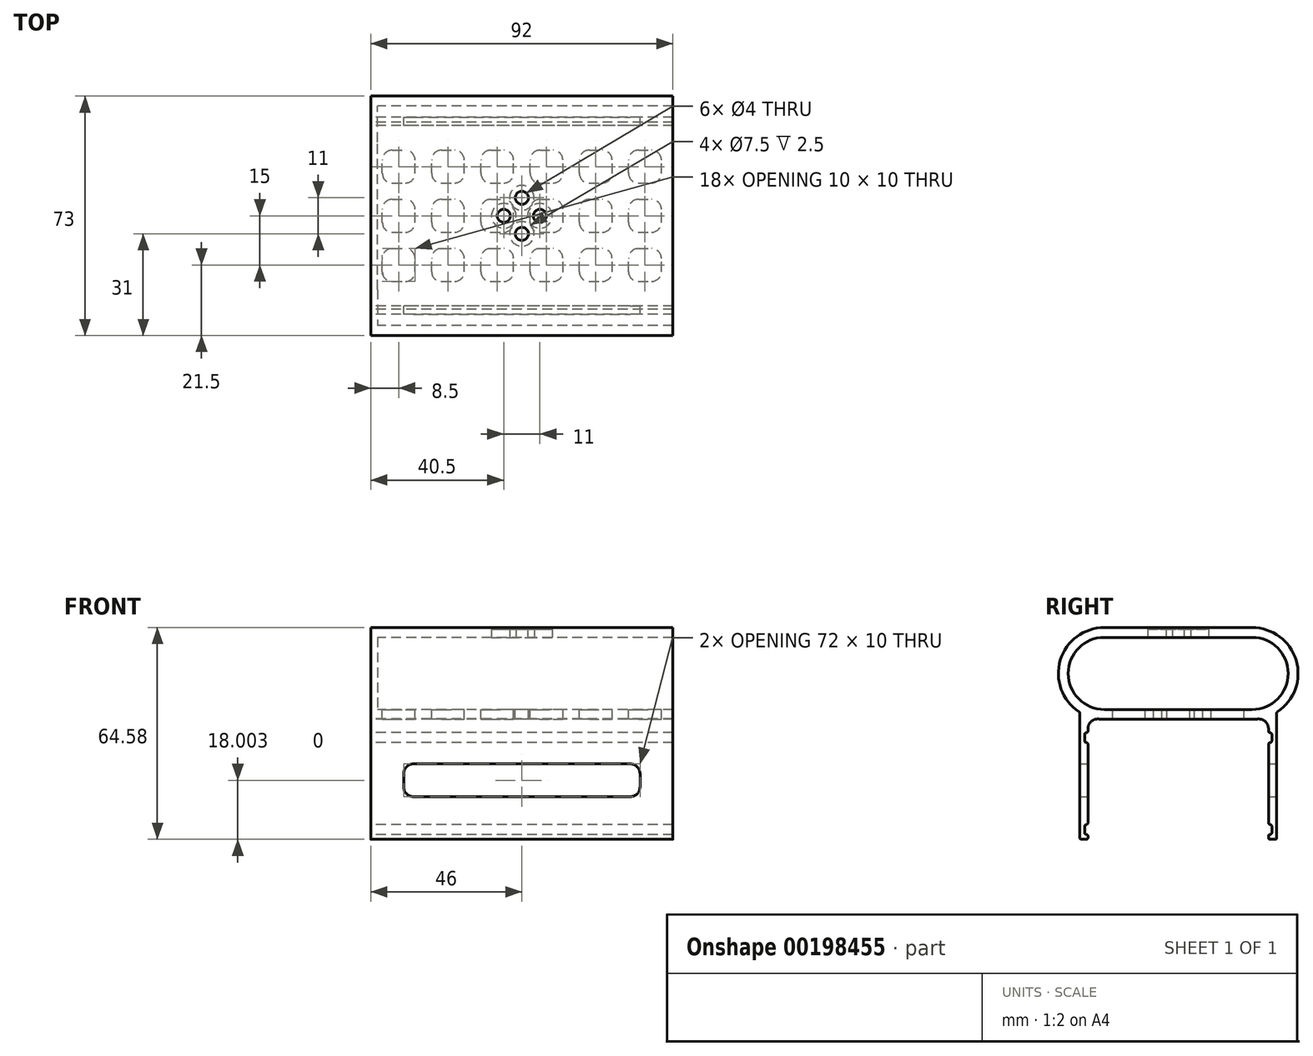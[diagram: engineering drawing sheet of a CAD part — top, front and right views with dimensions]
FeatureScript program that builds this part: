
annotation { "Feature Type Name" : "Feature", "Feature Type Description" : "" }
export const myFeature = defineFeature(function(context is Context, id is Id, definition is map)
    precondition{}
    {
        {
            var Q0;
            Q0=qCreatedBy(makeId("Right.planeOp"),FACE);
            var sketch = newSketch(context, id + "F0", { "sketchPlane" : qUnion([Q0])});
            skLineSegment(sketch, "E0.bottom", {"start": v(-22.5, 0) * mm, "end": v(22.5, 0) * mm});
            skLineSegment(sketch, "E0.top", {"start": v(-22.5, 22) * mm, "end": v(22.5, 22) * mm});
            skLineSegment(sketch, "E0.left", {"start": v(-33.5, 11) * mm, "end": v(-33.5, 11) * mm});
            skLineSegment(sketch, "E0.right", {"start": v(33.5, 11) * mm, "end": v(33.5, 11) * mm});
            skPoint(sketch, "E1.visualSharp", {"position": v(-33.5, 22) * mm});
            skArc(sketch, "E1.filletArc", {"start": v(-22.5, 22) * mm, "mid": v(-30.28, 18.78) * mm, "end": v(-33.5, 11) * mm});
            skPoint(sketch, "E2.visualSharp", {"position": v(-33.5, 0) * mm});
            skArc(sketch, "E2.filletArc", {"start": v(-33.5, 11) * mm, "mid": v(-30.28, 3.22) * mm, "end": v(-22.5, 0) * mm});
            skPoint(sketch, "E3.visualSharp", {"position": v(33.5, 0) * mm});
            skArc(sketch, "E3.filletArc", {"start": v(22.5, 0) * mm, "mid": v(30.28, 3.22) * mm, "end": v(33.5, 11) * mm});
            skPoint(sketch, "E4.visualSharp", {"position": v(33.5, 22) * mm});
            skArc(sketch, "E4.filletArc", {"start": v(33.5, 11) * mm, "mid": v(30.28, 18.78) * mm, "end": v(22.5, 22) * mm});
            skLineSegment(sketch, "E5.0", {"start": v(-22.5, 25) * mm, "end": v(22.5, 25) * mm});
            skArc(sketch, "E5.1", {"start": v(-36.5, 11) * mm, "mid": v(-34.83, 4.37) * mm, "end": v(-30.22, -0.68) * mm});
            skLineSegment(sketch, "E5.2", {"start": v(-22.5, -3) * mm, "end": v(22.5, -3) * mm});
            skArc(sketch, "E5.3", {"start": v(-22.5, 25) * mm, "mid": v(-32.4, 20.9) * mm, "end": v(-36.5, 11) * mm});
            skArc(sketch, "E5.5", {"start": v(36.5, 11) * mm, "mid": v(32.4, 20.9) * mm, "end": v(22.5, 25) * mm});
            skLineSegment(sketch, "E6", {"start": v(-28.5, -1.65) * mm, "end": v(-28.5, -38.08) * mm, "construction": true});
            skLineSegment(sketch, "E7", {"start": v(-28.5, -38.08) * mm, "end": v(28.5, -38.08) * mm, "construction": true});
            skLineSegment(sketch, "E8", {"start": v(28.5, -38.08) * mm, "end": v(28.5, -1.65) * mm, "construction": true});
            skLineSegment(sketch, "E9", {"start": v(0, 0) * mm, "end": v(0, -38.08) * mm, "construction": true});
            skLineSegment(sketch, "E10", {"start": v(-28, -7.08) * mm, "end": v(-28, -7.08) * mm});
            skLineSegment(sketch, "E11", {"start": v(-27.5, -6.58) * mm, "end": v(-27.5, -5.88) * mm});
            skLineSegment(sketch, "E12", {"start": v(-28, -35.08) * mm, "end": v(-28, -35.08) * mm});
            skLineSegment(sketch, "E13", {"start": v(-27.5, -34.58) * mm, "end": v(-27.5, -10.58) * mm});
            skLineSegment(sketch, "E14", {"start": v(-28, -10.08) * mm, "end": v(-28, -10.08) * mm});
            skLineSegment(sketch, "E15", {"start": v(-28, -38.08) * mm, "end": v(-28, -38.08) * mm});
            skLineSegment(sketch, "E16", {"start": v(-27.5, -38.58) * mm, "end": v(-27.5, -39.08) * mm});
            skLineSegment(sketch, "E17", {"start": v(-28, -39.58) * mm, "end": v(-29.5, -39.58) * mm});
            skLineSegment(sketch, "E18", {"start": v(-30, -39.08) * mm, "end": v(-30, -1.1) * mm});
            skLineSegment(sketch, "E19", {"start": v(-28.5, -7.58) * mm, "end": v(-28.5, -9.58) * mm});
            skLineSegment(sketch, "E20", {"start": v(-28.5, -35.58) * mm, "end": v(-28.5, -37.58) * mm});
            skArc(sketch, "E21.trimOffspring", {"start": v(-24.15, -2.9) * mm, "mid": v(-23.32, -2.98) * mm, "end": v(-22.5, -3) * mm});
            skPoint(sketch, "E22.visualSharp", {"position": v(-30, -0.82) * mm});
            skArc(sketch, "E22.filletArc", {"start": v(-30, -1.1) * mm, "mid": v(-30.06, -0.86) * mm, "end": v(-30.22, -0.68) * mm});
            skPoint(sketch, "E23.visualSharp", {"position": v(-27.5, -2.08) * mm});
            skArc(sketch, "E23.filletArc", {"start": v(-24.15, -2.9) * mm, "mid": v(-26.5, -3.64) * mm, "end": v(-27.5, -5.88) * mm});
            skPoint(sketch, "E24.visualSharp", {"position": v(-28.5, -7.08) * mm});
            skArc(sketch, "E24.filletArc", {"start": v(-28, -7.08) * mm, "mid": v(-28.35, -7.22) * mm, "end": v(-28.5, -7.58) * mm});
            skPoint(sketch, "E25.visualSharp", {"position": v(-28.5, -10.08) * mm});
            skArc(sketch, "E25.filletArc", {"start": v(-28.5, -9.58) * mm, "mid": v(-28.35, -9.93) * mm, "end": v(-28, -10.08) * mm});
            skPoint(sketch, "E26.visualSharp", {"position": v(-27.5, -10.08) * mm});
            skArc(sketch, "E26.filletArc", {"start": v(-27.5, -10.58) * mm, "mid": v(-27.65, -10.22) * mm, "end": v(-28, -10.08) * mm});
            skPoint(sketch, "E27.visualSharp", {"position": v(-27.5, -7.08) * mm});
            skArc(sketch, "E27.filletArc", {"start": v(-28, -7.08) * mm, "mid": v(-27.65, -6.93) * mm, "end": v(-27.5, -6.58) * mm});
            skPoint(sketch, "E28.visualSharp", {"position": v(-27.5, -35.08) * mm});
            skArc(sketch, "E28.filletArc", {"start": v(-28, -35.08) * mm, "mid": v(-27.65, -34.93) * mm, "end": v(-27.5, -34.58) * mm});
            skPoint(sketch, "E29.visualSharp", {"position": v(-28.5, -35.08) * mm});
            skArc(sketch, "E29.filletArc", {"start": v(-28, -35.08) * mm, "mid": v(-28.35, -35.22) * mm, "end": v(-28.5, -35.58) * mm});
            skPoint(sketch, "E30.visualSharp", {"position": v(-28.5, -38.08) * mm});
            skArc(sketch, "E30.filletArc", {"start": v(-28.5, -37.58) * mm, "mid": v(-28.35, -37.93) * mm, "end": v(-28, -38.08) * mm});
            skPoint(sketch, "E31.visualSharp", {"position": v(-27.5, -38.08) * mm});
            skArc(sketch, "E31.filletArc", {"start": v(-27.5, -38.58) * mm, "mid": v(-27.65, -38.22) * mm, "end": v(-28, -38.08) * mm});
            skPoint(sketch, "E32.visualSharp", {"position": v(-27.5, -39.58) * mm});
            skArc(sketch, "E32.filletArc", {"start": v(-28, -39.58) * mm, "mid": v(-27.65, -39.43) * mm, "end": v(-27.5, -39.08) * mm});
            skPoint(sketch, "E33.visualSharp", {"position": v(-30, -39.58) * mm});
            skArc(sketch, "E33.filletArc", {"start": v(-30, -39.08) * mm, "mid": v(-29.85, -39.43) * mm, "end": v(-29.5, -39.58) * mm});
            skArc(sketch, "E34.MirrorCS", {"start": v(27.5, -38.58) * mm, "mid": v(27.65, -38.22) * mm, "end": v(28, -38.08) * mm});
            skArc(sketch, "E35.MirrorCS", {"start": v(28.5, -37.58) * mm, "mid": v(28.35, -37.93) * mm, "end": v(28, -38.08) * mm});
            skLineSegment(sketch, "E36.MirrorCS", {"start": v(28.5, -35.58) * mm, "end": v(28.5, -37.58) * mm});
            skArc(sketch, "E37.MirrorCS", {"start": v(28, -35.08) * mm, "mid": v(28.35, -35.22) * mm, "end": v(28.5, -35.58) * mm});
            skLineSegment(sketch, "E38.MirrorCS", {"start": v(27.5, -38.58) * mm, "end": v(27.5, -39.08) * mm});
            skArc(sketch, "E39.MirrorCS", {"start": v(28, -39.58) * mm, "mid": v(27.65, -39.43) * mm, "end": v(27.5, -39.08) * mm});
            skLineSegment(sketch, "E40.MirrorCS", {"start": v(28, -39.58) * mm, "end": v(29.5, -39.58) * mm});
            skArc(sketch, "E41.MirrorCS", {"start": v(28, -35.08) * mm, "mid": v(27.65, -34.93) * mm, "end": v(27.5, -34.58) * mm});
            skArc(sketch, "E42.MirrorCS", {"start": v(30, -1.1) * mm, "mid": v(30.06, -0.86) * mm, "end": v(30.22, -0.68) * mm});
            skLineSegment(sketch, "E43.MirrorCS", {"start": v(27.5, -6.58) * mm, "end": v(27.5, -5.88) * mm});
            skArc(sketch, "E44.MirrorCS", {"start": v(28, -7.08) * mm, "mid": v(27.65, -6.93) * mm, "end": v(27.5, -6.58) * mm});
            skArc(sketch, "E45.MirrorCS", {"start": v(28.5, -9.58) * mm, "mid": v(28.35, -9.93) * mm, "end": v(28, -10.08) * mm});
            skArc(sketch, "E46.MirrorCS", {"start": v(30, -39.08) * mm, "mid": v(29.85, -39.43) * mm, "end": v(29.5, -39.58) * mm});
            skArc(sketch, "E47.MirrorCS", {"start": v(28, -7.08) * mm, "mid": v(28.35, -7.22) * mm, "end": v(28.5, -7.58) * mm});
            skLineSegment(sketch, "E48.MirrorCS", {"start": v(28.5, -7.58) * mm, "end": v(28.5, -9.58) * mm});
            skArc(sketch, "E49.MirrorCS", {"start": v(27.5, -10.58) * mm, "mid": v(27.65, -10.22) * mm, "end": v(28, -10.08) * mm});
            skArc(sketch, "E50.MirrorCS", {"start": v(24.15, -2.9) * mm, "mid": v(23.32, -2.98) * mm, "end": v(22.5, -3) * mm});
            skPoint(sketch, "E51.MirrorP", {"position": v(30, -39.58) * mm});
            skPoint(sketch, "E52.MirrorP", {"position": v(28.5, -38.08) * mm});
            skPoint(sketch, "E53.MirrorP", {"position": v(27.5, -2.08) * mm});
            skPoint(sketch, "E54.MirrorP", {"position": v(27.5, -38.08) * mm});
            skLineSegment(sketch, "E55.MirrorCS", {"start": v(28.5, -1.65) * mm, "end": v(28.5, -38.08) * mm, "construction": true});
            skPoint(sketch, "E56.MirrorP", {"position": v(28.5, -10.08) * mm});
            skLineSegment(sketch, "E57.MirrorCS", {"start": v(30, -39.08) * mm, "end": v(30, -1.1) * mm});
            skLineSegment(sketch, "E58.MirrorCS", {"start": v(28, -35.08) * mm, "end": v(28, -35.08) * mm});
            skPoint(sketch, "E59.MirrorP", {"position": v(27.5, -10.08) * mm});
            skLineSegment(sketch, "E60.MirrorCS", {"start": v(28, -7.08) * mm, "end": v(28, -7.08) * mm});
            skPoint(sketch, "E61.MirrorP", {"position": v(27.5, -7.08) * mm});
            skLineSegment(sketch, "E62.MirrorCS", {"start": v(28, -38.08) * mm, "end": v(28, -38.08) * mm});
            skArc(sketch, "E63.MirrorCS", {"start": v(24.15, -2.9) * mm, "mid": v(26.5, -3.64) * mm, "end": v(27.5, -5.88) * mm});
            skPoint(sketch, "E64.MirrorP", {"position": v(27.5, -39.58) * mm});
            skPoint(sketch, "E65.MirrorP", {"position": v(28.5, -7.08) * mm});
            skPoint(sketch, "E66.MirrorP", {"position": v(28.5, -35.08) * mm});
            skLineSegment(sketch, "E67.MirrorCS", {"start": v(27.5, -34.58) * mm, "end": v(27.5, -10.58) * mm});
            skPoint(sketch, "E68.MirrorP", {"position": v(27.5, -35.08) * mm});
            skLineSegment(sketch, "E69.MirrorCS", {"start": v(28, -10.08) * mm, "end": v(28, -10.08) * mm});
            skPoint(sketch, "E70.MirrorP", {"position": v(30, -0.82) * mm});
            skArc(sketch, "E71.trimOffspring", {"start": v(30, -0.82) * mm, "mid": v(34.77, 4.25) * mm, "end": v(36.5, 11) * mm});
            skSolve(sketch);
        }
        {
            var Q0;
            Q0 = qSketchRegion(id + "F0", true);
            extrude(context, id + "F1", {"entities" : qUnion([Q0]), "depth" : 90 * mm});
        }
        {
            var Q0;
            Q0=makeQuery(id+"F1.opExtrude","CAP_FACE",FACE,{"disambiguationData":[OSD([sQuery(id+"F0.wireOp",EDGE,"E0.bottom"),sQuery(id+"F0.wireOp",EDGE,"E0.top"),sQuery(id+"F0.wireOp",EDGE,"E1.filletArc"),sQuery(id+"F0.wireOp",EDGE,"E2.filletArc"),sQuery(id+"F0.wireOp",EDGE,"E3.filletArc"),sQuery(id+"F0.wireOp",EDGE,"E4.filletArc"),sQuery(id+"F0.wireOp",EDGE,"E5.0"),sQuery(id+"F0.wireOp",EDGE,"E5.1"),sQuery(id+"F0.wireOp",EDGE,"E5.2"),sQuery(id+"F0.wireOp",EDGE,"E5.3"),sQuery(id+"F0.wireOp",EDGE,"E5.4"),sQuery(id+"F0.wireOp",EDGE,"E5.5")])],"isStart":true});
            var sketch = newSketch(context, id + "F2", { "sketchPlane" : qUnion([Q0])});
            skArc(sketch, "E72.0", {"start": v(-30.22, -0.68) * mm, "mid": v(-35.9, 15.03) * mm, "end": v(-22.5, 25) * mm});
            skArc(sketch, "E73.0.0", {"start": v(-30.22, -0.68) * mm, "mid": v(-30.06, -0.86) * mm, "end": v(-30, -1.1) * mm});
            skLineSegment(sketch, "E73.0.1", {"start": v(-30, -1.1) * mm, "end": v(-30, -39.08) * mm});
            skArc(sketch, "E73.0.2", {"start": v(-30, -39.08) * mm, "mid": v(-29.85, -39.43) * mm, "end": v(-29.5, -39.58) * mm});
            skLineSegment(sketch, "E73.0.3", {"start": v(-29.5, -39.58) * mm, "end": v(-28, -39.58) * mm});
            skArc(sketch, "E73.0.4", {"start": v(-28, -39.58) * mm, "mid": v(-27.65, -39.43) * mm, "end": v(-27.5, -39.08) * mm});
            skLineSegment(sketch, "E73.0.5", {"start": v(-27.5, -39.08) * mm, "end": v(-27.5, -38.58) * mm});
            skArc(sketch, "E73.0.6", {"start": v(-27.5, -38.58) * mm, "mid": v(-27.65, -38.22) * mm, "end": v(-28, -38.08) * mm});
            skArc(sketch, "E73.0.7", {"start": v(-28, -38.08) * mm, "mid": v(-28.35, -37.93) * mm, "end": v(-28.5, -37.58) * mm});
            skLineSegment(sketch, "E73.0.8", {"start": v(-28.5, -37.58) * mm, "end": v(-28.5, -35.58) * mm});
            skArc(sketch, "E73.0.9", {"start": v(-28.5, -35.58) * mm, "mid": v(-28.35, -35.22) * mm, "end": v(-28, -35.08) * mm});
            skArc(sketch, "E73.0.10", {"start": v(-28, -35.08) * mm, "mid": v(-27.65, -34.93) * mm, "end": v(-27.5, -34.58) * mm});
            skLineSegment(sketch, "E73.0.11", {"start": v(-27.5, -34.58) * mm, "end": v(-27.5, -10.58) * mm});
            skArc(sketch, "E73.0.12", {"start": v(-27.5, -10.58) * mm, "mid": v(-27.65, -10.22) * mm, "end": v(-28, -10.08) * mm});
            skArc(sketch, "E73.0.13", {"start": v(-28, -10.08) * mm, "mid": v(-28.35, -9.93) * mm, "end": v(-28.5, -9.58) * mm});
            skLineSegment(sketch, "E73.0.14", {"start": v(-28.5, -9.58) * mm, "end": v(-28.5, -7.58) * mm});
            skArc(sketch, "E73.0.15", {"start": v(-28.5, -7.58) * mm, "mid": v(-28.35, -7.22) * mm, "end": v(-28, -7.08) * mm});
            skArc(sketch, "E73.0.16", {"start": v(-28, -7.08) * mm, "mid": v(-27.65, -6.93) * mm, "end": v(-27.5, -6.58) * mm});
            skLineSegment(sketch, "E73.0.17", {"start": v(-27.5, -6.58) * mm, "end": v(-27.5, -5.88) * mm});
            skArc(sketch, "E73.0.18", {"start": v(-27.5, -5.88) * mm, "mid": v(-26.5, -3.64) * mm, "end": v(-24.15, -2.9) * mm});
            skArc(sketch, "E73.0.19", {"start": v(-24.15, -2.9) * mm, "mid": v(-23.32, -2.98) * mm, "end": v(-22.5, -3) * mm});
            skLineSegment(sketch, "E73.0.20", {"start": v(-22.5, -3) * mm, "end": v(22.5, -3) * mm});
            skArc(sketch, "E73.0.21", {"start": v(22.5, -3) * mm, "mid": v(23.32, -2.98) * mm, "end": v(24.15, -2.9) * mm});
            skArc(sketch, "E73.0.22", {"start": v(24.15, -2.9) * mm, "mid": v(26.5, -3.64) * mm, "end": v(27.5, -5.88) * mm});
            skLineSegment(sketch, "E73.0.23", {"start": v(27.5, -5.88) * mm, "end": v(27.5, -6.58) * mm});
            skArc(sketch, "E73.0.24", {"start": v(27.5, -6.58) * mm, "mid": v(27.65, -6.93) * mm, "end": v(28, -7.08) * mm});
            skArc(sketch, "E73.0.25", {"start": v(28, -7.08) * mm, "mid": v(28.35, -7.22) * mm, "end": v(28.5, -7.58) * mm});
            skLineSegment(sketch, "E73.0.26", {"start": v(28.5, -7.58) * mm, "end": v(28.5, -9.58) * mm});
            skArc(sketch, "E73.0.27", {"start": v(28.5, -9.58) * mm, "mid": v(28.35, -9.93) * mm, "end": v(28, -10.08) * mm});
            skArc(sketch, "E73.0.28", {"start": v(28, -10.08) * mm, "mid": v(27.65, -10.22) * mm, "end": v(27.5, -10.58) * mm});
            skLineSegment(sketch, "E73.0.29", {"start": v(27.5, -10.58) * mm, "end": v(27.5, -34.58) * mm});
            skArc(sketch, "E73.0.30", {"start": v(27.5, -34.58) * mm, "mid": v(27.65, -34.93) * mm, "end": v(28, -35.08) * mm});
            skArc(sketch, "E73.0.31", {"start": v(28, -35.08) * mm, "mid": v(28.35, -35.22) * mm, "end": v(28.5, -35.58) * mm});
            skLineSegment(sketch, "E73.0.32", {"start": v(28.5, -35.58) * mm, "end": v(28.5, -37.58) * mm});
            skArc(sketch, "E73.0.33", {"start": v(28.5, -37.58) * mm, "mid": v(28.35, -37.93) * mm, "end": v(28, -38.08) * mm});
            skArc(sketch, "E73.0.34", {"start": v(28, -38.08) * mm, "mid": v(27.65, -38.22) * mm, "end": v(27.5, -38.58) * mm});
            skLineSegment(sketch, "E73.0.35", {"start": v(27.5, -38.58) * mm, "end": v(27.5, -39.08) * mm});
            skArc(sketch, "E73.0.36", {"start": v(27.5, -39.08) * mm, "mid": v(27.65, -39.43) * mm, "end": v(28, -39.58) * mm});
            skLineSegment(sketch, "E73.0.37", {"start": v(28, -39.58) * mm, "end": v(29.5, -39.58) * mm});
            skArc(sketch, "E73.0.38", {"start": v(29.5, -39.58) * mm, "mid": v(29.85, -39.43) * mm, "end": v(30, -39.08) * mm});
            skLineSegment(sketch, "E73.0.39", {"start": v(30, -39.08) * mm, "end": v(30, -1.1) * mm});
            skArc(sketch, "E73.0.40", {"start": v(30, -1.1) * mm, "mid": v(30.06, -0.86) * mm, "end": v(30.22, -0.68) * mm});
            skArc(sketch, "E73.0.41", {"start": v(30.22, -0.68) * mm, "mid": v(35.9, 15.03) * mm, "end": v(22.5, 25) * mm});
            skLineSegment(sketch, "E73.0.42", {"start": v(22.5, 25) * mm, "end": v(-22.5, 25) * mm});
            skArc(sketch, "E73.0.43", {"start": v(-22.5, 25) * mm, "mid": v(-35.9, 15.03) * mm, "end": v(-30.22, -0.68) * mm});
            skSolve(sketch);
        }
        {
            var Q0;
            Q0 = qSketchRegion(id + "F2", true);
            extrude(context, id + "F3", {"entities" : qUnion([Q0]), "operationType" : NewBodyOperationType.ADD, "depth" : 2 * mm});
        }
        {
            var Q0;
            Q0=qCreatedBy(makeId("Top.planeOp"),FACE);
            var sketch = newSketch(context, id + "F4", { "sketchPlane" : qUnion([Q0])});
            skLineSegment(sketch, "E74.bottom", {"start": v(4.5, -5) * mm, "end": v(8.5, -5) * mm});
            skLineSegment(sketch, "E74.top", {"start": v(4.5, 5) * mm, "end": v(8.5, 5) * mm});
            skLineSegment(sketch, "E74.left", {"start": v(1.5, -2) * mm, "end": v(1.5, 2) * mm});
            skLineSegment(sketch, "E74.right", {"start": v(11.5, -2) * mm, "end": v(11.5, 2) * mm});
            skPoint(sketch, "E74.middle", {"position": v(6.5, 0) * mm});
            skPoint(sketch, "E75.visualSharp", {"position": v(1.5, 5) * mm});
            skArc(sketch, "E75.filletArc", {"start": v(4.5, 5) * mm, "mid": v(2.38, 4.12) * mm, "end": v(1.5, 2) * mm});
            skPoint(sketch, "E76.visualSharp", {"position": v(11.5, 5) * mm});
            skArc(sketch, "E76.filletArc", {"start": v(11.5, 2) * mm, "mid": v(10.62, 4.12) * mm, "end": v(8.5, 5) * mm});
            skPoint(sketch, "E77.visualSharp", {"position": v(11.5, -5) * mm});
            skArc(sketch, "E77.filletArc", {"start": v(8.5, -5) * mm, "mid": v(10.62, -4.12) * mm, "end": v(11.5, -2) * mm});
            skPoint(sketch, "E78.visualSharp", {"position": v(1.5, -5) * mm});
            skArc(sketch, "E78.filletArc", {"start": v(1.5, -2) * mm, "mid": v(2.38, -4.12) * mm, "end": v(4.5, -5) * mm});
            skPoint(sketch, "E79.0.1.0", {"position": v(1.5, 20) * mm});
            skLineSegment(sketch, "E79.0.1.1", {"start": v(1.5, 13) * mm, "end": v(1.5, 17) * mm});
            skLineSegment(sketch, "E79.0.1.2", {"start": v(11.5, 13) * mm, "end": v(11.5, 17) * mm});
            skPoint(sketch, "E79.0.1.3", {"position": v(11.5, 20) * mm});
            skPoint(sketch, "E79.0.1.4", {"position": v(6.5, 15) * mm});
            skPoint(sketch, "E79.0.1.5", {"position": v(11.5, 10) * mm});
            skPoint(sketch, "E79.0.1.6", {"position": v(1.5, 10) * mm});
            skArc(sketch, "E79.0.1.7", {"start": v(4.5, 20) * mm, "mid": v(2.38, 19.12) * mm, "end": v(1.5, 17) * mm});
            skArc(sketch, "E79.0.1.8", {"start": v(1.5, 13) * mm, "mid": v(2.38, 10.88) * mm, "end": v(4.5, 10) * mm});
            skLineSegment(sketch, "E79.0.1.9", {"start": v(4.5, 10) * mm, "end": v(8.5, 10) * mm});
            skLineSegment(sketch, "E79.0.1.10", {"start": v(4.5, 20) * mm, "end": v(8.5, 20) * mm});
            skArc(sketch, "E79.0.1.11", {"start": v(11.5, 17) * mm, "mid": v(10.62, 19.12) * mm, "end": v(8.5, 20) * mm});
            skArc(sketch, "E79.0.1.12", {"start": v(8.5, 10) * mm, "mid": v(10.62, 10.88) * mm, "end": v(11.5, 13) * mm});
            skPoint(sketch, "E79.1.0.0", {"position": v(16.5, 5) * mm});
            skLineSegment(sketch, "E79.1.0.1", {"start": v(16.5, -2) * mm, "end": v(16.5, 2) * mm});
            skLineSegment(sketch, "E79.1.0.2", {"start": v(26.5, -2) * mm, "end": v(26.5, 2) * mm});
            skPoint(sketch, "E79.1.0.3", {"position": v(26.5, 5) * mm});
            skPoint(sketch, "E79.1.0.4", {"position": v(21.5, 0) * mm});
            skPoint(sketch, "E79.1.0.5", {"position": v(26.5, -5) * mm});
            skPoint(sketch, "E79.1.0.6", {"position": v(16.5, -5) * mm});
            skArc(sketch, "E79.1.0.7", {"start": v(19.5, 5) * mm, "mid": v(17.38, 4.12) * mm, "end": v(16.5, 2) * mm});
            skArc(sketch, "E79.1.0.8", {"start": v(16.5, -2) * mm, "mid": v(17.38, -4.12) * mm, "end": v(19.5, -5) * mm});
            skLineSegment(sketch, "E79.1.0.9", {"start": v(19.5, -5) * mm, "end": v(23.5, -5) * mm});
            skLineSegment(sketch, "E79.1.0.10", {"start": v(19.5, 5) * mm, "end": v(23.5, 5) * mm});
            skArc(sketch, "E79.1.0.11", {"start": v(26.5, 2) * mm, "mid": v(25.62, 4.12) * mm, "end": v(23.5, 5) * mm});
            skArc(sketch, "E79.1.0.12", {"start": v(23.5, -5) * mm, "mid": v(25.62, -4.12) * mm, "end": v(26.5, -2) * mm});
            skPoint(sketch, "E79.1.1.0", {"position": v(16.5, 20) * mm});
            skLineSegment(sketch, "E79.1.1.1", {"start": v(16.5, 13) * mm, "end": v(16.5, 17) * mm});
            skLineSegment(sketch, "E79.1.1.2", {"start": v(26.5, 13) * mm, "end": v(26.5, 17) * mm});
            skPoint(sketch, "E79.1.1.3", {"position": v(26.5, 20) * mm});
            skPoint(sketch, "E79.1.1.4", {"position": v(21.5, 15) * mm});
            skPoint(sketch, "E79.1.1.5", {"position": v(26.5, 10) * mm});
            skPoint(sketch, "E79.1.1.6", {"position": v(16.5, 10) * mm});
            skArc(sketch, "E79.1.1.7", {"start": v(19.5, 20) * mm, "mid": v(17.38, 19.12) * mm, "end": v(16.5, 17) * mm});
            skArc(sketch, "E79.1.1.8", {"start": v(16.5, 13) * mm, "mid": v(17.38, 10.88) * mm, "end": v(19.5, 10) * mm});
            skLineSegment(sketch, "E79.1.1.9", {"start": v(19.5, 10) * mm, "end": v(23.5, 10) * mm});
            skLineSegment(sketch, "E79.1.1.10", {"start": v(19.5, 20) * mm, "end": v(23.5, 20) * mm});
            skArc(sketch, "E79.1.1.11", {"start": v(26.5, 17) * mm, "mid": v(25.62, 19.12) * mm, "end": v(23.5, 20) * mm});
            skArc(sketch, "E79.1.1.12", {"start": v(23.5, 10) * mm, "mid": v(25.62, 10.88) * mm, "end": v(26.5, 13) * mm});
            skPoint(sketch, "E79.2.0.0", {"position": v(31.5, 5) * mm});
            skLineSegment(sketch, "E79.2.0.1", {"start": v(31.5, -2) * mm, "end": v(31.5, 2) * mm});
            skLineSegment(sketch, "E79.2.0.2", {"start": v(41.5, -2) * mm, "end": v(41.5, 2) * mm});
            skPoint(sketch, "E79.2.0.3", {"position": v(41.5, 5) * mm});
            skPoint(sketch, "E79.2.0.4", {"position": v(36.5, 0) * mm});
            skPoint(sketch, "E79.2.0.5", {"position": v(41.5, -5) * mm});
            skPoint(sketch, "E79.2.0.6", {"position": v(31.5, -5) * mm});
            skArc(sketch, "E79.2.0.7", {"start": v(34.5, 5) * mm, "mid": v(32.38, 4.12) * mm, "end": v(31.5, 2) * mm});
            skArc(sketch, "E79.2.0.8", {"start": v(31.5, -2) * mm, "mid": v(32.38, -4.12) * mm, "end": v(34.5, -5) * mm});
            skLineSegment(sketch, "E79.2.0.9", {"start": v(34.5, -5) * mm, "end": v(38.5, -5) * mm});
            skLineSegment(sketch, "E79.2.0.10", {"start": v(34.5, 5) * mm, "end": v(38.5, 5) * mm});
            skArc(sketch, "E79.2.0.11", {"start": v(41.5, 2) * mm, "mid": v(40.62, 4.12) * mm, "end": v(38.5, 5) * mm});
            skArc(sketch, "E79.2.0.12", {"start": v(38.5, -5) * mm, "mid": v(40.62, -4.12) * mm, "end": v(41.5, -2) * mm});
            skPoint(sketch, "E79.2.1.0", {"position": v(31.5, 20) * mm});
            skLineSegment(sketch, "E79.2.1.1", {"start": v(31.5, 13) * mm, "end": v(31.5, 17) * mm});
            skLineSegment(sketch, "E79.2.1.2", {"start": v(41.5, 13) * mm, "end": v(41.5, 17) * mm});
            skPoint(sketch, "E79.2.1.3", {"position": v(41.5, 20) * mm});
            skPoint(sketch, "E79.2.1.4", {"position": v(36.5, 15) * mm});
            skPoint(sketch, "E79.2.1.5", {"position": v(41.5, 10) * mm});
            skPoint(sketch, "E79.2.1.6", {"position": v(31.5, 10) * mm});
            skArc(sketch, "E79.2.1.7", {"start": v(34.5, 20) * mm, "mid": v(32.38, 19.12) * mm, "end": v(31.5, 17) * mm});
            skArc(sketch, "E79.2.1.8", {"start": v(31.5, 13) * mm, "mid": v(32.38, 10.88) * mm, "end": v(34.5, 10) * mm});
            skLineSegment(sketch, "E79.2.1.9", {"start": v(34.5, 10) * mm, "end": v(38.5, 10) * mm});
            skLineSegment(sketch, "E79.2.1.10", {"start": v(34.5, 20) * mm, "end": v(38.5, 20) * mm});
            skArc(sketch, "E79.2.1.11", {"start": v(41.5, 17) * mm, "mid": v(40.62, 19.12) * mm, "end": v(38.5, 20) * mm});
            skArc(sketch, "E79.2.1.12", {"start": v(38.5, 10) * mm, "mid": v(40.62, 10.88) * mm, "end": v(41.5, 13) * mm});
            skPoint(sketch, "E79.3.0.0", {"position": v(46.5, 5) * mm});
            skLineSegment(sketch, "E79.3.0.1", {"start": v(46.5, -2) * mm, "end": v(46.5, 2) * mm});
            skLineSegment(sketch, "E79.3.0.2", {"start": v(56.5, -2) * mm, "end": v(56.5, 2) * mm});
            skPoint(sketch, "E79.3.0.3", {"position": v(56.5, 5) * mm});
            skPoint(sketch, "E79.3.0.4", {"position": v(51.5, 0) * mm});
            skPoint(sketch, "E79.3.0.5", {"position": v(56.5, -5) * mm});
            skPoint(sketch, "E79.3.0.6", {"position": v(46.5, -5) * mm});
            skArc(sketch, "E79.3.0.7", {"start": v(49.5, 5) * mm, "mid": v(47.38, 4.12) * mm, "end": v(46.5, 2) * mm});
            skArc(sketch, "E79.3.0.8", {"start": v(46.5, -2) * mm, "mid": v(47.38, -4.12) * mm, "end": v(49.5, -5) * mm});
            skLineSegment(sketch, "E79.3.0.9", {"start": v(49.5, -5) * mm, "end": v(53.5, -5) * mm});
            skLineSegment(sketch, "E79.3.0.10", {"start": v(49.5, 5) * mm, "end": v(53.5, 5) * mm});
            skArc(sketch, "E79.3.0.11", {"start": v(56.5, 2) * mm, "mid": v(55.62, 4.12) * mm, "end": v(53.5, 5) * mm});
            skArc(sketch, "E79.3.0.12", {"start": v(53.5, -5) * mm, "mid": v(55.62, -4.12) * mm, "end": v(56.5, -2) * mm});
            skPoint(sketch, "E79.3.1.0", {"position": v(46.5, 20) * mm});
            skLineSegment(sketch, "E79.3.1.1", {"start": v(46.5, 13) * mm, "end": v(46.5, 17) * mm});
            skLineSegment(sketch, "E79.3.1.2", {"start": v(56.5, 13) * mm, "end": v(56.5, 17) * mm});
            skPoint(sketch, "E79.3.1.3", {"position": v(56.5, 20) * mm});
            skPoint(sketch, "E79.3.1.4", {"position": v(51.5, 15) * mm});
            skPoint(sketch, "E79.3.1.5", {"position": v(56.5, 10) * mm});
            skPoint(sketch, "E79.3.1.6", {"position": v(46.5, 10) * mm});
            skArc(sketch, "E79.3.1.7", {"start": v(49.5, 20) * mm, "mid": v(47.38, 19.12) * mm, "end": v(46.5, 17) * mm});
            skArc(sketch, "E79.3.1.8", {"start": v(46.5, 13) * mm, "mid": v(47.38, 10.88) * mm, "end": v(49.5, 10) * mm});
            skLineSegment(sketch, "E79.3.1.9", {"start": v(49.5, 10) * mm, "end": v(53.5, 10) * mm});
            skLineSegment(sketch, "E79.3.1.10", {"start": v(49.5, 20) * mm, "end": v(53.5, 20) * mm});
            skArc(sketch, "E79.3.1.11", {"start": v(56.5, 17) * mm, "mid": v(55.62, 19.12) * mm, "end": v(53.5, 20) * mm});
            skArc(sketch, "E79.3.1.12", {"start": v(53.5, 10) * mm, "mid": v(55.62, 10.88) * mm, "end": v(56.5, 13) * mm});
            skPoint(sketch, "E79.4.0.0", {"position": v(61.5, 5) * mm});
            skLineSegment(sketch, "E79.4.0.1", {"start": v(61.5, -2) * mm, "end": v(61.5, 2) * mm});
            skLineSegment(sketch, "E79.4.0.2", {"start": v(71.5, -2) * mm, "end": v(71.5, 2) * mm});
            skPoint(sketch, "E79.4.0.3", {"position": v(71.5, 5) * mm});
            skPoint(sketch, "E79.4.0.4", {"position": v(66.5, 0) * mm});
            skPoint(sketch, "E79.4.0.5", {"position": v(71.5, -5) * mm});
            skPoint(sketch, "E79.4.0.6", {"position": v(61.5, -5) * mm});
            skArc(sketch, "E79.4.0.7", {"start": v(64.5, 5) * mm, "mid": v(62.38, 4.12) * mm, "end": v(61.5, 2) * mm});
            skArc(sketch, "E79.4.0.8", {"start": v(61.5, -2) * mm, "mid": v(62.38, -4.12) * mm, "end": v(64.5, -5) * mm});
            skLineSegment(sketch, "E79.4.0.9", {"start": v(64.5, -5) * mm, "end": v(68.5, -5) * mm});
            skLineSegment(sketch, "E79.4.0.10", {"start": v(64.5, 5) * mm, "end": v(68.5, 5) * mm});
            skArc(sketch, "E79.4.0.11", {"start": v(71.5, 2) * mm, "mid": v(70.62, 4.12) * mm, "end": v(68.5, 5) * mm});
            skArc(sketch, "E79.4.0.12", {"start": v(68.5, -5) * mm, "mid": v(70.62, -4.12) * mm, "end": v(71.5, -2) * mm});
            skPoint(sketch, "E79.4.1.0", {"position": v(61.5, 20) * mm});
            skLineSegment(sketch, "E79.4.1.1", {"start": v(61.5, 13) * mm, "end": v(61.5, 17) * mm});
            skLineSegment(sketch, "E79.4.1.2", {"start": v(71.5, 13) * mm, "end": v(71.5, 17) * mm});
            skPoint(sketch, "E79.4.1.3", {"position": v(71.5, 20) * mm});
            skPoint(sketch, "E79.4.1.4", {"position": v(66.5, 15) * mm});
            skPoint(sketch, "E79.4.1.5", {"position": v(71.5, 10) * mm});
            skPoint(sketch, "E79.4.1.6", {"position": v(61.5, 10) * mm});
            skArc(sketch, "E79.4.1.7", {"start": v(64.5, 20) * mm, "mid": v(62.38, 19.12) * mm, "end": v(61.5, 17) * mm});
            skArc(sketch, "E79.4.1.8", {"start": v(61.5, 13) * mm, "mid": v(62.38, 10.88) * mm, "end": v(64.5, 10) * mm});
            skLineSegment(sketch, "E79.4.1.9", {"start": v(64.5, 10) * mm, "end": v(68.5, 10) * mm});
            skLineSegment(sketch, "E79.4.1.10", {"start": v(64.5, 20) * mm, "end": v(68.5, 20) * mm});
            skArc(sketch, "E79.4.1.11", {"start": v(71.5, 17) * mm, "mid": v(70.62, 19.12) * mm, "end": v(68.5, 20) * mm});
            skArc(sketch, "E79.4.1.12", {"start": v(68.5, 10) * mm, "mid": v(70.62, 10.88) * mm, "end": v(71.5, 13) * mm});
            skPoint(sketch, "E79.5.0.0", {"position": v(76.5, 5) * mm});
            skLineSegment(sketch, "E79.5.0.1", {"start": v(76.5, -2) * mm, "end": v(76.5, 2) * mm});
            skLineSegment(sketch, "E79.5.0.2", {"start": v(86.5, -2) * mm, "end": v(86.5, 2) * mm});
            skPoint(sketch, "E79.5.0.3", {"position": v(86.5, 5) * mm});
            skPoint(sketch, "E79.5.0.4", {"position": v(81.5, 0) * mm});
            skPoint(sketch, "E79.5.0.5", {"position": v(86.5, -5) * mm});
            skPoint(sketch, "E79.5.0.6", {"position": v(76.5, -5) * mm});
            skArc(sketch, "E79.5.0.7", {"start": v(79.5, 5) * mm, "mid": v(77.38, 4.12) * mm, "end": v(76.5, 2) * mm});
            skArc(sketch, "E79.5.0.8", {"start": v(76.5, -2) * mm, "mid": v(77.38, -4.12) * mm, "end": v(79.5, -5) * mm});
            skLineSegment(sketch, "E79.5.0.9", {"start": v(79.5, -5) * mm, "end": v(83.5, -5) * mm});
            skLineSegment(sketch, "E79.5.0.10", {"start": v(79.5, 5) * mm, "end": v(83.5, 5) * mm});
            skArc(sketch, "E79.5.0.11", {"start": v(86.5, 2) * mm, "mid": v(85.62, 4.12) * mm, "end": v(83.5, 5) * mm});
            skArc(sketch, "E79.5.0.12", {"start": v(83.5, -5) * mm, "mid": v(85.62, -4.12) * mm, "end": v(86.5, -2) * mm});
            skPoint(sketch, "E79.5.1.0", {"position": v(76.5, 20) * mm});
            skLineSegment(sketch, "E79.5.1.1", {"start": v(76.5, 13) * mm, "end": v(76.5, 17) * mm});
            skLineSegment(sketch, "E79.5.1.2", {"start": v(86.5, 13) * mm, "end": v(86.5, 17) * mm});
            skPoint(sketch, "E79.5.1.3", {"position": v(86.5, 20) * mm});
            skPoint(sketch, "E79.5.1.4", {"position": v(81.5, 15) * mm});
            skPoint(sketch, "E79.5.1.5", {"position": v(86.5, 10) * mm});
            skPoint(sketch, "E79.5.1.6", {"position": v(76.5, 10) * mm});
            skArc(sketch, "E79.5.1.7", {"start": v(79.5, 20) * mm, "mid": v(77.38, 19.12) * mm, "end": v(76.5, 17) * mm});
            skArc(sketch, "E79.5.1.8", {"start": v(76.5, 13) * mm, "mid": v(77.38, 10.88) * mm, "end": v(79.5, 10) * mm});
            skLineSegment(sketch, "E79.5.1.9", {"start": v(79.5, 10) * mm, "end": v(83.5, 10) * mm});
            skLineSegment(sketch, "E79.5.1.10", {"start": v(79.5, 20) * mm, "end": v(83.5, 20) * mm});
            skArc(sketch, "E79.5.1.11", {"start": v(86.5, 17) * mm, "mid": v(85.62, 19.12) * mm, "end": v(83.5, 20) * mm});
            skArc(sketch, "E79.5.1.12", {"start": v(83.5, 10) * mm, "mid": v(85.62, 10.88) * mm, "end": v(86.5, 13) * mm});
            skLineSegment(sketch, "E79.direction1", {"start": v(10, -10) * mm, "end": v(25, -10) * mm, "construction": true});
            skLineSegment(sketch, "E79.direction2", {"start": v(10, -10) * mm, "end": v(10, 5) * mm, "construction": true});
            skLineSegment(sketch, "E80.0.1.0", {"start": v(10, -25) * mm, "end": v(10, -10) * mm, "construction": true});
            skPoint(sketch, "E80.0.1.1", {"position": v(81.5, -15) * mm});
            skPoint(sketch, "E80.0.1.2", {"position": v(61.5, -20) * mm});
            skLineSegment(sketch, "E80.0.1.3", {"start": v(10, -25) * mm, "end": v(25, -25) * mm, "construction": true});
            skPoint(sketch, "E80.0.1.4", {"position": v(86.5, -20) * mm});
            skPoint(sketch, "E80.0.1.5", {"position": v(76.5, -20) * mm});
            skPoint(sketch, "E80.0.1.6", {"position": v(6.5, -15) * mm});
            skPoint(sketch, "E80.0.1.7", {"position": v(1.5, -10) * mm});
            skPoint(sketch, "E80.0.1.8", {"position": v(16.5, -10) * mm});
            skPoint(sketch, "E80.0.1.9", {"position": v(26.5, -10) * mm});
            skPoint(sketch, "E80.0.1.10", {"position": v(11.5, -10) * mm});
            skPoint(sketch, "E80.0.1.11", {"position": v(31.5, -10) * mm});
            skPoint(sketch, "E80.0.1.12", {"position": v(21.5, -15) * mm});
            skPoint(sketch, "E80.0.1.13", {"position": v(41.5, -10) * mm});
            skPoint(sketch, "E80.0.1.14", {"position": v(26.5, -20) * mm});
            skPoint(sketch, "E80.0.1.15", {"position": v(11.5, -20) * mm});
            skPoint(sketch, "E80.0.1.16", {"position": v(46.5, -10) * mm});
            skPoint(sketch, "E80.0.1.17", {"position": v(36.5, -15) * mm});
            skPoint(sketch, "E80.0.1.18", {"position": v(16.5, -20) * mm});
            skPoint(sketch, "E80.0.1.19", {"position": v(71.5, -10) * mm});
            skPoint(sketch, "E80.0.1.20", {"position": v(56.5, -20) * mm});
            skPoint(sketch, "E80.0.1.21", {"position": v(56.5, -10) * mm});
            skPoint(sketch, "E80.0.1.22", {"position": v(41.5, -20) * mm});
            skPoint(sketch, "E80.0.1.23", {"position": v(1.5, -20) * mm});
            skPoint(sketch, "E80.0.1.24", {"position": v(66.5, -15) * mm});
            skPoint(sketch, "E80.0.1.25", {"position": v(46.5, -20) * mm});
            skPoint(sketch, "E80.0.1.26", {"position": v(76.5, -10) * mm});
            skPoint(sketch, "E80.0.1.27", {"position": v(51.5, -15) * mm});
            skPoint(sketch, "E80.0.1.28", {"position": v(31.5, -20) * mm});
            skPoint(sketch, "E80.0.1.29", {"position": v(61.5, -10) * mm});
            skPoint(sketch, "E80.0.1.30", {"position": v(71.5, -20) * mm});
            skPoint(sketch, "E80.0.1.31", {"position": v(86.5, -10) * mm});
            skArc(sketch, "E80.0.1.32", {"start": v(34.5, -10) * mm, "mid": v(32.38, -10.88) * mm, "end": v(31.5, -13) * mm});
            skArc(sketch, "E80.0.1.33", {"start": v(19.5, -10) * mm, "mid": v(17.38, -10.88) * mm, "end": v(16.5, -13) * mm});
            skArc(sketch, "E80.0.1.34", {"start": v(79.5, -10) * mm, "mid": v(77.38, -10.88) * mm, "end": v(76.5, -13) * mm});
            skArc(sketch, "E80.0.1.35", {"start": v(64.5, -10) * mm, "mid": v(62.38, -10.88) * mm, "end": v(61.5, -13) * mm});
            skArc(sketch, "E80.0.1.36", {"start": v(49.5, -10) * mm, "mid": v(47.38, -10.88) * mm, "end": v(46.5, -13) * mm});
            skArc(sketch, "E80.0.1.37", {"start": v(31.5, -17) * mm, "mid": v(32.38, -19.12) * mm, "end": v(34.5, -20) * mm});
            skArc(sketch, "E80.0.1.38", {"start": v(16.5, -17) * mm, "mid": v(17.38, -19.12) * mm, "end": v(19.5, -20) * mm});
            skArc(sketch, "E80.0.1.39", {"start": v(76.5, -17) * mm, "mid": v(77.38, -19.12) * mm, "end": v(79.5, -20) * mm});
            skArc(sketch, "E80.0.1.40", {"start": v(61.5, -17) * mm, "mid": v(62.38, -19.12) * mm, "end": v(64.5, -20) * mm});
            skArc(sketch, "E80.0.1.41", {"start": v(46.5, -17) * mm, "mid": v(47.38, -19.12) * mm, "end": v(49.5, -20) * mm});
            skArc(sketch, "E80.0.1.42", {"start": v(41.5, -13) * mm, "mid": v(40.62, -10.88) * mm, "end": v(38.5, -10) * mm});
            skArc(sketch, "E80.0.1.43", {"start": v(26.5, -13) * mm, "mid": v(25.62, -10.88) * mm, "end": v(23.5, -10) * mm});
            skArc(sketch, "E80.0.1.44", {"start": v(86.5, -13) * mm, "mid": v(85.62, -10.88) * mm, "end": v(83.5, -10) * mm});
            skArc(sketch, "E80.0.1.45", {"start": v(71.5, -13) * mm, "mid": v(70.62, -10.88) * mm, "end": v(68.5, -10) * mm});
            skArc(sketch, "E80.0.1.46", {"start": v(56.5, -13) * mm, "mid": v(55.62, -10.88) * mm, "end": v(53.5, -10) * mm});
            skArc(sketch, "E80.0.1.47", {"start": v(68.5, -20) * mm, "mid": v(70.62, -19.12) * mm, "end": v(71.5, -17) * mm});
            skArc(sketch, "E80.0.1.48", {"start": v(53.5, -20) * mm, "mid": v(55.62, -19.12) * mm, "end": v(56.5, -17) * mm});
            skArc(sketch, "E80.0.1.49", {"start": v(38.5, -20) * mm, "mid": v(40.62, -19.12) * mm, "end": v(41.5, -17) * mm});
            skArc(sketch, "E80.0.1.50", {"start": v(23.5, -20) * mm, "mid": v(25.62, -19.12) * mm, "end": v(26.5, -17) * mm});
            skArc(sketch, "E80.0.1.51", {"start": v(83.5, -20) * mm, "mid": v(85.62, -19.12) * mm, "end": v(86.5, -17) * mm});
            skArc(sketch, "E80.0.1.52", {"start": v(4.5, -10) * mm, "mid": v(2.38, -10.88) * mm, "end": v(1.5, -13) * mm});
            skArc(sketch, "E80.0.1.53", {"start": v(8.5, -20) * mm, "mid": v(10.62, -19.12) * mm, "end": v(11.5, -17) * mm});
            skArc(sketch, "E80.0.1.54", {"start": v(1.5, -17) * mm, "mid": v(2.38, -19.12) * mm, "end": v(4.5, -20) * mm});
            skLineSegment(sketch, "E80.0.1.55", {"start": v(86.5, -17) * mm, "end": v(86.5, -13) * mm});
            skLineSegment(sketch, "E80.0.1.56", {"start": v(71.5, -17) * mm, "end": v(71.5, -13) * mm});
            skLineSegment(sketch, "E80.0.1.57", {"start": v(31.5, -17) * mm, "end": v(31.5, -13) * mm});
            skLineSegment(sketch, "E80.0.1.58", {"start": v(16.5, -17) * mm, "end": v(16.5, -13) * mm});
            skLineSegment(sketch, "E80.0.1.59", {"start": v(46.5, -17) * mm, "end": v(46.5, -13) * mm});
            skLineSegment(sketch, "E80.0.1.60", {"start": v(61.5, -17) * mm, "end": v(61.5, -13) * mm});
            skLineSegment(sketch, "E80.0.1.61", {"start": v(76.5, -17) * mm, "end": v(76.5, -13) * mm});
            skLineSegment(sketch, "E80.0.1.62", {"start": v(56.5, -17) * mm, "end": v(56.5, -13) * mm});
            skLineSegment(sketch, "E80.0.1.63", {"start": v(41.5, -17) * mm, "end": v(41.5, -13) * mm});
            skLineSegment(sketch, "E80.0.1.64", {"start": v(26.5, -17) * mm, "end": v(26.5, -13) * mm});
            skLineSegment(sketch, "E80.0.1.65", {"start": v(34.5, -20) * mm, "end": v(38.5, -20) * mm});
            skLineSegment(sketch, "E80.0.1.66", {"start": v(19.5, -20) * mm, "end": v(23.5, -20) * mm});
            skLineSegment(sketch, "E80.0.1.67", {"start": v(79.5, -20) * mm, "end": v(83.5, -20) * mm});
            skLineSegment(sketch, "E80.0.1.68", {"start": v(64.5, -20) * mm, "end": v(68.5, -20) * mm});
            skLineSegment(sketch, "E80.0.1.69", {"start": v(49.5, -20) * mm, "end": v(53.5, -20) * mm});
            skLineSegment(sketch, "E80.0.1.70", {"start": v(34.5, -10) * mm, "end": v(38.5, -10) * mm});
            skLineSegment(sketch, "E80.0.1.71", {"start": v(19.5, -10) * mm, "end": v(23.5, -10) * mm});
            skLineSegment(sketch, "E80.0.1.72", {"start": v(79.5, -10) * mm, "end": v(83.5, -10) * mm});
            skLineSegment(sketch, "E80.0.1.73", {"start": v(64.5, -10) * mm, "end": v(68.5, -10) * mm});
            skLineSegment(sketch, "E80.0.1.74", {"start": v(49.5, -10) * mm, "end": v(53.5, -10) * mm});
            skLineSegment(sketch, "E80.0.1.75", {"start": v(4.5, -20) * mm, "end": v(8.5, -20) * mm});
            skLineSegment(sketch, "E80.0.1.76", {"start": v(4.5, -10) * mm, "end": v(8.5, -10) * mm});
            skLineSegment(sketch, "E80.0.1.77", {"start": v(1.5, -17) * mm, "end": v(1.5, -13) * mm});
            skLineSegment(sketch, "E80.0.1.78", {"start": v(11.5, -17) * mm, "end": v(11.5, -13) * mm});
            skArc(sketch, "E80.0.1.79", {"start": v(11.5, -13) * mm, "mid": v(10.62, -10.88) * mm, "end": v(8.5, -10) * mm});
            skLineSegment(sketch, "E80.direction1", {"start": v(1.5, -5) * mm, "end": v(26.5, -5) * mm, "construction": true});
            skLineSegment(sketch, "E80.direction2", {"start": v(1.5, -5) * mm, "end": v(1.5, -20) * mm, "construction": true});
            skSolve(sketch);
        }
        {
            var Q0;
            Q0 = qSketchRegion(id + "F4", true);
            extrude(context, id + "F5", {"entities" : qUnion([Q0]), "operationType" : NewBodyOperationType.REMOVE, "endBound" : BoundingType.THROUGH_ALL, "oppositeDirection" : true, "depth" : 25 * mm});
        }
        {
            var Q0;
            Q0=makeQuery(id+"F3.boolean.opBoolean","MERGE",FACE,{"derivedFrom":[makeQuery(id+"F1.opExtrude","SWEPT_FACE",FACE,{"disambiguationData":[OSD([sQuery(id+"F0.wireOp",EDGE,"E5.0")])]}),makeQuery(id+"F3.opExtrude","SWEPT_FACE",FACE,{"disambiguationData":[OSD([sQuery(id+"F2.wireOp",EDGE,"E73.0.42")])]})]});
            var sketch = newSketch(context, id + "F6", { "sketchPlane" : qUnion([Q0])});
            skCircle(sketch, "E81", {"center": v(38.5, 0) * mm, "radius": 2 * mm});
            skCircle(sketch, "E82.1.0", {"center": v(44, -5.5) * mm, "radius": 2 * mm});
            skCircle(sketch, "E82.2.0", {"center": v(49.5, 0) * mm, "radius": 2 * mm});
            skCircle(sketch, "E82.3.0", {"center": v(44, 5.5) * mm, "radius": 2 * mm});
            skPoint(sketch, "E82.center", {"position": v(44, 0) * mm});
            skLineSegment(sketch, "E83", {"start": v(-2, 0) * mm, "end": v(90, 0) * mm, "construction": true});
            skSolve(sketch);
        }
        {
            var Q0;
            Q0 = qSketchRegion(id + "F6", true);
            extrude(context, id + "F7", {"entities" : qUnion([Q0]), "operationType" : NewBodyOperationType.REMOVE, "endBound" : BoundingType.THROUGH_ALL, "oppositeDirection" : true, "depth" : 25 * mm});
        }
        {
            var Q0;
            Q0=makeQuery(id+"F1.opExtrude","SWEPT_FACE",FACE,{"disambiguationData":[OSD([sQuery(id+"F0.wireOp",EDGE,"E0.top")])]});
            var sketch = newSketch(context, id + "F8", { "sketchPlane" : qUnion([Q0])});
            skPoint(sketch, "E84", {"position": v(44, -5.5) * mm});
            skPoint(sketch, "E85", {"position": v(44, 5.5) * mm});
            skPoint(sketch, "E86", {"position": v(38.5, 0) * mm});
            skPoint(sketch, "E87", {"position": v(49.5, 0) * mm});
            skSolve(sketch);
        }
        {
            var Q0;
            Q0=sQuery(id+"F8.wireOp",VERTEX,"E84");
            var Q1;
            Q1=sQuery(id+"F8.wireOp",VERTEX,"E86");
            var Q2;
            Q2=sQuery(id+"F8.wireOp",VERTEX,"E87");
            var Q3;
            Q3=sQuery(id+"F8.wireOp",VERTEX,"E85");
            var Q4;
            Q4=makeQuery(id+"F1.opExtrude","SWEPT_BODY",BODY,{"disambiguationData":[OSD([sQuery(id+"F0.wireOp",EDGE,"E0.bottom"),sQuery(id+"F0.wireOp",EDGE,"E0.top"),sQuery(id+"F0.wireOp",EDGE,"E1.filletArc"),sQuery(id+"F0.wireOp",EDGE,"E2.filletArc"),sQuery(id+"F0.wireOp",EDGE,"E3.filletArc"),sQuery(id+"F0.wireOp",EDGE,"E4.filletArc"),sQuery(id+"F0.wireOp",EDGE,"E5.0"),sQuery(id+"F0.wireOp",EDGE,"E5.1"),sQuery(id+"F0.wireOp",EDGE,"E5.2"),sQuery(id+"F0.wireOp",EDGE,"E5.3"),sQuery(id+"F0.wireOp",EDGE,"E5.5"),sQuery(id+"F0.wireOp",EDGE,"E11"),sQuery(id+"F0.wireOp",EDGE,"E13"),sQuery(id+"F0.wireOp",EDGE,"E16"),sQuery(id+"F0.wireOp",EDGE,"E17"),sQuery(id+"F0.wireOp",EDGE,"E18"),sQuery(id+"F0.wireOp",EDGE,"E19"),sQuery(id+"F0.wireOp",EDGE,"E20"),sQuery(id+"F0.wireOp",EDGE,"E21.trimOffspring"),sQuery(id+"F0.wireOp",EDGE,"E22.filletArc"),sQuery(id+"F0.wireOp",EDGE,"E23.filletArc"),sQuery(id+"F0.wireOp",EDGE,"E24.filletArc"),sQuery(id+"F0.wireOp",EDGE,"E25.filletArc"),sQuery(id+"F0.wireOp",EDGE,"E26.filletArc"),sQuery(id+"F0.wireOp",EDGE,"E27.filletArc"),sQuery(id+"F0.wireOp",EDGE,"E28.filletArc"),sQuery(id+"F0.wireOp",EDGE,"E29.filletArc"),sQuery(id+"F0.wireOp",EDGE,"E30.filletArc"),sQuery(id+"F0.wireOp",EDGE,"E31.filletArc"),sQuery(id+"F0.wireOp",EDGE,"E32.filletArc"),sQuery(id+"F0.wireOp",EDGE,"E33.filletArc"),sQuery(id+"F0.wireOp",EDGE,"E34.MirrorCS"),sQuery(id+"F0.wireOp",EDGE,"E35.MirrorCS"),sQuery(id+"F0.wireOp",EDGE,"E36.MirrorCS"),sQuery(id+"F0.wireOp",EDGE,"E37.MirrorCS"),sQuery(id+"F0.wireOp",EDGE,"E38.MirrorCS"),sQuery(id+"F0.wireOp",EDGE,"E39.MirrorCS"),sQuery(id+"F0.wireOp",EDGE,"E40.MirrorCS"),sQuery(id+"F0.wireOp",EDGE,"E41.MirrorCS"),sQuery(id+"F0.wireOp",EDGE,"E42.MirrorCS"),sQuery(id+"F0.wireOp",EDGE,"E43.MirrorCS"),sQuery(id+"F0.wireOp",EDGE,"E44.MirrorCS"),sQuery(id+"F0.wireOp",EDGE,"E45.MirrorCS"),sQuery(id+"F0.wireOp",EDGE,"E46.MirrorCS"),sQuery(id+"F0.wireOp",EDGE,"E47.MirrorCS"),sQuery(id+"F0.wireOp",EDGE,"E48.MirrorCS"),sQuery(id+"F0.wireOp",EDGE,"E49.MirrorCS"),sQuery(id+"F0.wireOp",EDGE,"E50.MirrorCS"),sQuery(id+"F0.wireOp",EDGE,"E57.MirrorCS"),sQuery(id+"F0.wireOp",EDGE,"E63.MirrorCS"),sQuery(id+"F0.wireOp",EDGE,"E67.MirrorCS"),sQuery(id+"F0.wireOp",EDGE,"E71.trimOffspring")])]});
            hole(context, id + "F9", {"style" : HoleStyle.C_BORE, "endStyle" : HoleEndStyle.THROUGH, "holeDiameter" : 4 * mm, "cBoreDiameter" : 7.5 * mm, "cBoreDepth" : 2.5 * mm, "locations" : qUnion([Q0, Q1, Q2, Q3]), "scope" : qUnion([Q4]), "isTappedThrough" : true});
        }
        {
            var Q0;
            Q0=makeQuery(id+"F3.boolean.opBoolean","MERGE",FACE,{"derivedFrom":[makeQuery(id+"F1.opExtrude","SWEPT_FACE",FACE,{"disambiguationData":[OSD([sQuery(id+"F0.wireOp",EDGE,"E57.MirrorCS")])]}),makeQuery(id+"F3.opExtrude","SWEPT_FACE",FACE,{"disambiguationData":[OSD([sQuery(id+"F2.wireOp",EDGE,"E73.0.1")])]})]});
            var sketch = newSketch(context, id + "F10", { "sketchPlane" : qUnion([Q0])});
            skLineSegment(sketch, "E88.bottom", {"start": v(-11, -26.58) * mm, "end": v(-77, -26.58) * mm});
            skLineSegment(sketch, "E88.top", {"start": v(-11, -16.58) * mm, "end": v(-77, -16.58) * mm});
            skLineSegment(sketch, "E88.left", {"start": v(-8, -23.58) * mm, "end": v(-8, -19.58) * mm});
            skLineSegment(sketch, "E88.right", {"start": v(-80, -23.58) * mm, "end": v(-80, -19.58) * mm});
            skPoint(sketch, "E89.visualSharp", {"position": v(-8, -26.58) * mm});
            skArc(sketch, "E89.filletArc", {"start": v(-11, -26.58) * mm, "mid": v(-8.88, -25.7) * mm, "end": v(-8, -23.58) * mm});
            skPoint(sketch, "E90.visualSharp", {"position": v(-8, -16.58) * mm});
            skArc(sketch, "E90.filletArc", {"start": v(-8, -19.58) * mm, "mid": v(-8.88, -17.46) * mm, "end": v(-11, -16.58) * mm});
            skPoint(sketch, "E91.visualSharp", {"position": v(-80, -16.58) * mm});
            skArc(sketch, "E91.filletArc", {"start": v(-77, -16.58) * mm, "mid": v(-79.12, -17.46) * mm, "end": v(-80, -19.58) * mm});
            skPoint(sketch, "E92.visualSharp", {"position": v(-80, -26.58) * mm});
            skArc(sketch, "E92.filletArc", {"start": v(-80, -23.58) * mm, "mid": v(-79.12, -25.7) * mm, "end": v(-77, -26.58) * mm});
            skSolve(sketch);
        }
        {
            var Q0;
            Q0 = qSketchRegion(id + "F10", true);
            var Q1;
            Q1=makeQuery(id+"F3.boolean.opBoolean","MERGE",FACE,{"derivedFrom":[makeQuery(id+"F1.opExtrude","SWEPT_FACE",FACE,{"disambiguationData":[OSD([sQuery(id+"F0.wireOp",EDGE,"E18")])]}),makeQuery(id+"F3.opExtrude","SWEPT_FACE",FACE,{"disambiguationData":[OSD([sQuery(id+"F2.wireOp",EDGE,"E73.0.39")])]})]});
            extrude(context, id + "F11", {"entities" : qUnion([Q0]), "operationType" : NewBodyOperationType.REMOVE, "endBound" : BoundingType.UP_TO_SURFACE, "oppositeDirection" : true, "endBoundEntityFace" : qUnion([Q1]), "depth" : 25 * mm});
        }
    });
